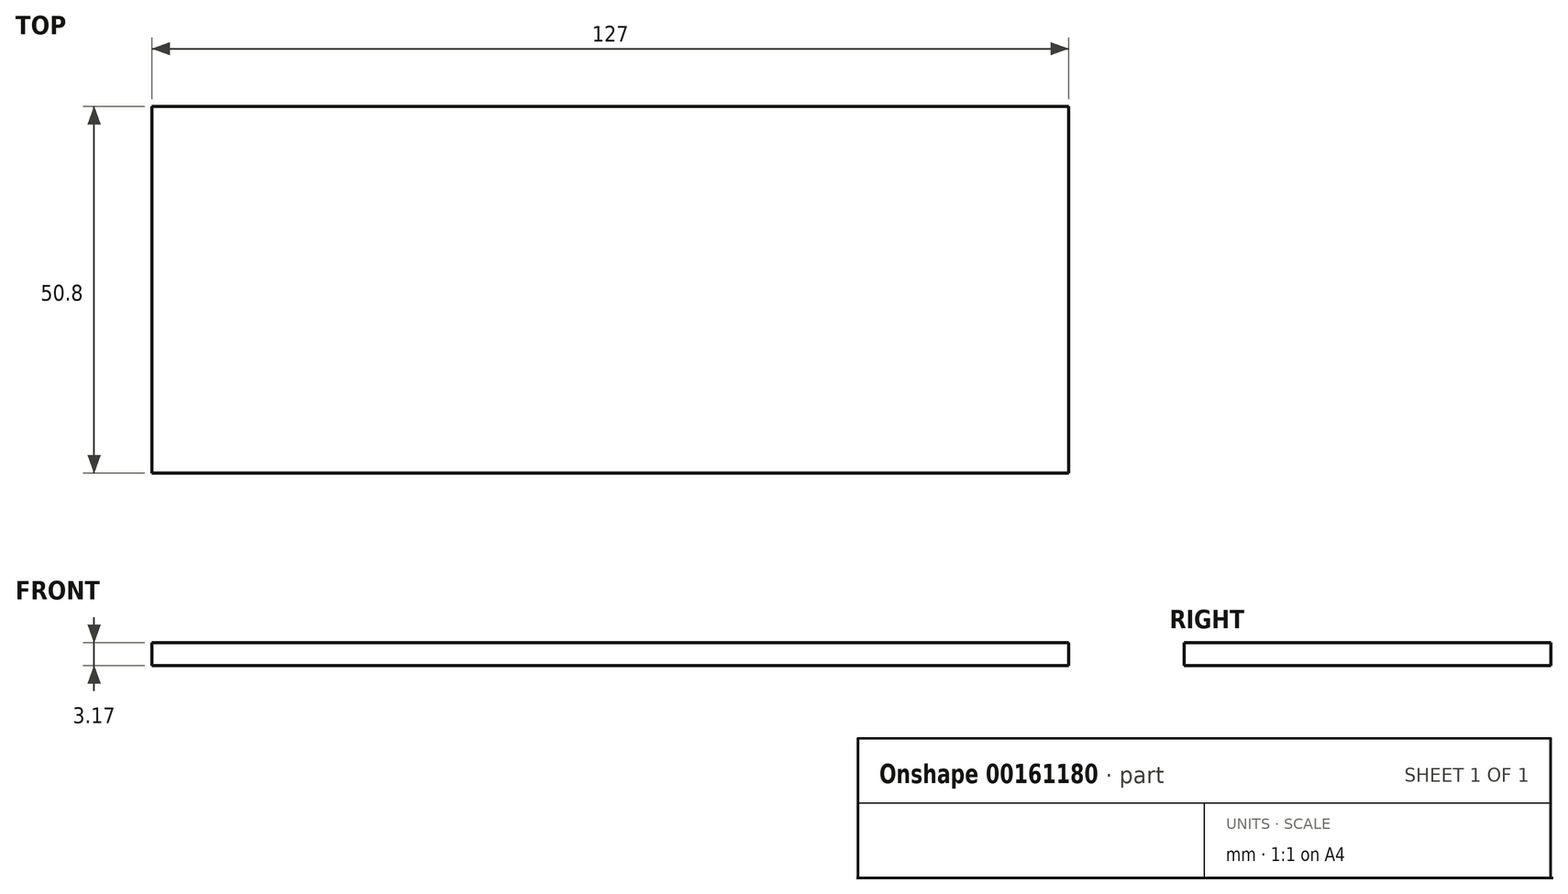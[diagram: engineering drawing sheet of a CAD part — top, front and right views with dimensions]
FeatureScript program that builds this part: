
annotation { "Feature Type Name" : "Feature", "Feature Type Description" : "" }
export const myFeature = defineFeature(function(context is Context, id is Id, definition is map)
    precondition{}
    {
        {
            var Q0;
            Q0=qCreatedBy(makeId("Top.planeOp"),FACE);
            var sketch = newSketch(context, id + "F0", { "sketchPlane" : qUnion([Q0])});
            skLineSegment(sketch, "E0.bottom", {"start": v(-63.5, 25.4) * mm, "end": v(63.5, 25.4) * mm});
            skLineSegment(sketch, "E0.top", {"start": v(-63.5, -25.4) * mm, "end": v(63.5, -25.4) * mm});
            skLineSegment(sketch, "E0.left", {"start": v(-63.5, 25.4) * mm, "end": v(-63.5, -25.4) * mm});
            skLineSegment(sketch, "E0.right", {"start": v(63.5, 25.4) * mm, "end": v(63.5, -25.4) * mm});
            skPoint(sketch, "E0.middle", {"position": v(0, 0) * mm});
            skSolve(sketch);
        }
        {
            var Q0;
            Q0 = qSketchRegion(id + "F0", true);
            extrude(context, id + "F1", {"entities" : qUnion([Q0]), "depth" : 3.17 * mm});
        }
    });
